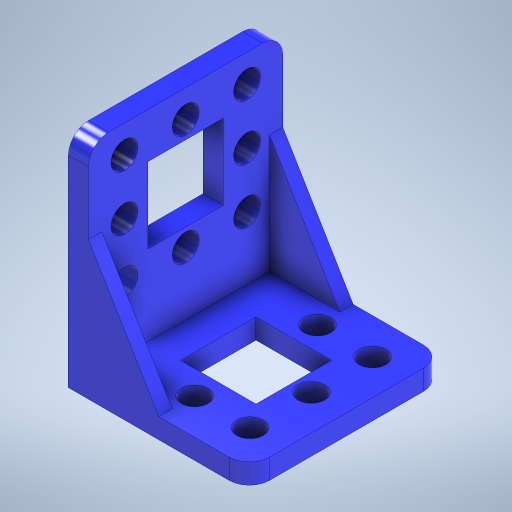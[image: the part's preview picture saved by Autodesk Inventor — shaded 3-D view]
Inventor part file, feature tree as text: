
AUTODESK INVENTOR PART (.ipt)
format: ipt  version: 2023.1 (Build 271208000, 208)  size: 381,952 bytes
history: native  units: mm
features: extrude x4, sketch x4, fillet x2
ambient origin geometry x8: Origin, YZ Plane, XZ Plane, XY Plane, X Axis, Y Axis, Z Axis, Center Point
bodies: Solid1 (feature_tree)
feature tree (10):
  extrude  "Extrusion1"  Depth=27.0mm
  fillet  "Fillet1"  Radius=13.5mm
  extrude  "Extrusion2"  Depth=11.25mm
  fillet  "Fillet2"  Radius=11.25mm
  extrude  "Extrusion3"  Depth=5.625mm
  extrude  "Extrusion4"  Depth=8.25mm
  sketch  "Sketch1"  dims[d0=29.0mm d1=27.0mm d2=13.5mm]
  sketch  "Sketch2"  dims[d3=14.5mm d4=11.25mm d5=11.25mm]
  sketch  "Sketch3"  dims[d6=5.625mm d7=5.625mm]
  sketch  "Sketch4"  dims[d8=4.0mm d9=5.25mm d10=4.0mm d12=5.35mm d13=4.125mm d14=3.0mm d15=0.0mm d16=3.0mm d17=29.0mm d18=33.0mm d19=11.25mm d20=11.25mm d21=12.0mm d22=8.875mm d23=2.625mm d24=4.0mm d25=2.625mm d26=4.0mm d27=5.35mm d28=0.0mm d29=5.625mm d30=5.625mm d31=8.25mm d32=4.125mm d33=3.0mm d34=0.0mm d35=3.0mm d36=2.0mm d37=0.0mm d38=2.0mm d39=0.0mm d40=9.15mm d41=8.25mm]
